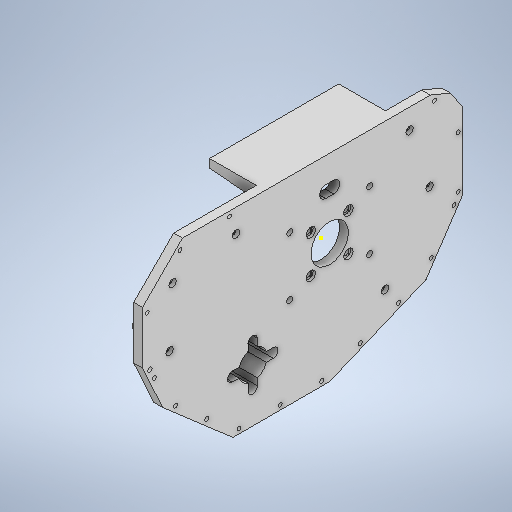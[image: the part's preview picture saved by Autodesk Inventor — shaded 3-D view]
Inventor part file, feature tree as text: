
AUTODESK INVENTOR PART (.ipt)
format: ipt  version: 2025.2 (Build 292293000, 293)  size: 1,278,464 bytes
history: native  units: mm
features: sketch x23, reference x23, projected_geometry x19, extrude x17, chamfer x5, other x5, fillet x2
ambient origin geometry x8: Origin, YZ Plane, XZ Plane, XY Plane, X Axis, Y Axis, Z Axis, Center Point
bodies: body_side (feature_tree), Solid1 (feature_tree)
feature tree (94):
  extrude  "Extrusion1"  Depth=76.5mm
  extrude  "Extrusion2"  Depth=4.0mm
  chamfer  "Chamfer1"  Distance=40.0mm Angle=360.0deg
  fillet  "Fillet1"  Radius=7.15585mm
  extrude  "Extrusion3"  Depth=7.1mm TaperAngle=360.0deg
  extrude  "Extrusion4"  Depth=21.7mm TaperAngle=360.0deg
  extrude  "Extrusion5"  Depth=28.0mm
  extrude  "Extrusion6"  Depth=35.5mm TaperAngle=0.0deg
  extrude  "Extrusion7"  Depth=3.0mm TaperAngle=45.0deg
  extrude  "Extrusion8"  Depth=40.1mm
  extrude  "Extrusion9"  TaperAngle=0.0deg  [1 undecoded]
  sketch  "Sketch15"  dims[d62=30.0mm d63=22.0mm]
  chamfer  "Chamfer2"  Distance=40.0mm Angle=360.0deg
  chamfer  "Chamfer3"  [1 undecoded]
  chamfer  "Chamfer4"  Distance=20.5mm
  extrude  "Extrusion11"  Depth=3.0mm
  extrude  "Extrusion12"  Depth=1.5mm
  chamfer  "Chamfer5"  [1 undecoded]
  fillet  "Fillet5"  Radius=4.45mm
  extrude  "Extrusion13"  Depth=22.0mm
  extrude  "Extrusion14"  Depth=6.0mm
  extrude  "Extrusion15"  Depth=90.0mm
  extrude  "Extrusion16"  Depth=50.0mm
  extrude  "Extrusion17"  Depth=117.0mm
  extrude  "Extrusion18"  Depth=92.0mm
  sketch  "Sketch1"  dims[d0=7.15585mm d1=76.5mm]
  sketch  "Sketch Circular Pattern2"  dims[d2=40.0mm d3=4.0mm]
  sketch  "Sketch Circular Pattern3"  dims[d18=7.1mm d19=40.0mm d21=360.0deg]
  sketch  "Sketch Circular Pattern4"  dims[d28=10.85mm d29=28.0mm]
  sketch  "Sketch2"  dims[d8=45.0deg d9=40.0mm d11=360.0deg d14=7.15585mm]
  sketch  "Sketch3"  dims[d23=21.7mm d24=40.0mm d26=360.0deg]
  sketch  "Sketch4"  dims[d31=6.6mm d32=0.0mm d33=35.5mm d34=0.0mm]
  sketch  "Sketch5"  dims[d35=43.0mm d36=3.0mm d37=35.5mm d38=45.0deg]
  sketch  "Sketch Circular Pattern5"  dims[d39=3.0mm d40=40.1mm]
  sketch  "Sketch6"  dims[d41=28.0mm d42=0.0mm d43=0.0mm d44=0.0mm]
  projected_geometry  "Projected Loop1"
  projected_geometry  "Projected Loop2"
  projected_geometry  "Projected Loop3"
  projected_geometry  "Projected Loop4"
  sketch  "Sketch7"  dims[d52=30.9mm d53=20.5mm d54=0.0mm]
  sketch  "Sketch8"  dims[d55=18.0mm d56=3.0mm]
  sketch  "Sketch13"  dims[d57=6.0mm d58=1.5mm d59=0.0mm d60=0.0mm d61=4.45mm]
  sketch  "Sketch16"  dims[d64=6.0mm d65=0.0mm d66=180.0mm]
  projected_geometry  "Projected Loop5"
  sketch  "Sketch18"  dims[d67=90.0mm d68=92.0mm]
  reference  "Reference3"
  reference  "Reference4"
  reference  "Reference5"
  reference  "Reference6"
  reference  "Reference7"
  reference  "Reference8"
  reference  "Reference9"
  reference  "Reference10"
  reference  "Reference11"
  reference  "Reference12"
  reference  "Reference13"
  reference  "Reference14"
  reference  "Reference15"
  reference  "Reference16"
  reference  "Reference18"
  reference  "Reference19"
  reference  "Reference20"
  reference  "Reference21"
  reference  "Reference22"
  reference  "Reference23"
  reference  "Reference24"
  sketch  "Sketch19"  dims[d85=100.0mm d86=50.0mm]
  reference  "Reference25"
  reference  "Reference26"
  sketch  "Sketch20"  dims[d87=30.0mm d88=117.0mm]
  sketch  "Sketch21"  dims[d89=45.0deg d90=92.0mm]
  sketch  "Sketch22"  dims[d91=45.0mm]
  projected_geometry  "Projected Loop6"
  sketch  "Sketch Circular Pattern6"  dims[d45=4.0mm d46=40.0mm d48=360.0deg d50=0.0mm d51=0.0mm]
  projected_geometry  "Projected Loop7"
  projected_geometry  "Projected Loop8"
  projected_geometry  "Projected Loop9"
  sketch  "Sketch23"  dims[d92=52.0mm]
  projected_geometry  "Projected Loop10"
  projected_geometry  "Projected Loop11"
  projected_geometry  "Projected Loop12"
  projected_geometry  "Projected Loop13"
  sketch  "Sketch24"  dims[d93=10.0mm d94=2.5mm d95=10.0mm d96=0.0mm d104=30.0mm d105=2.0mm d106=45.0deg d107=20.0mm d108=2.0mm d109=45.0deg d110=10.0mm d111=2.0mm d112=45.0deg d113=35.0mm d114=0.0mm d115=92.0mm d116=2.5mm d117=3.3mm d118=0.0mm d119=0.0mm d120=3.0mm d121=35.0mm d122=45.0deg d123=4.0mm d124=3.0mm d125=3.0mm d126=3.0mm d127=3.0mm d128=3.0mm d129=3.0mm d130=0.0mm d131=0.0mm d132=5.6mm d133=5.6mm d134=5.6mm d135=5.6mm d136=5.6mm d137=5.6mm d138=3.0mm d139=0.0mm d140=7.1mm d141=7.1mm d142=7.1mm d143=7.1mm d144=2.0mm d145=0.0mm d146=40.0mm d148=360.0deg d150=0.2mm d151=0.0mm d152=0.2mm d153=0.0mm d154=0.2mm d155=0.0mm]
  projected_geometry  "Projected Loop14"
  projected_geometry  "Projected Loop15"
  projected_geometry  "Projected Loop16"
  projected_geometry  "Projected Loop17"
  projected_geometry  "Projected Loop18"
  projected_geometry  "Projected Loop19"
  parser-record x1  (decoder bookkeeping rows leaked as tree rows — omitted from the tree; the rows remain in map.json)
  other  "WBR.iam"
  other  "inner_body_c:1"
  other  "inner_body_b:1"
  other  "OUT_SHELL:1"
note: 3 required parameter values undecoded (feature->parameter linkage not recoverable at this tier; creation-order binding heuristic only, values carry confidence <= 0.55)
note: 1 file-system path scrubbed to <path> (originals preserved in map.json)
